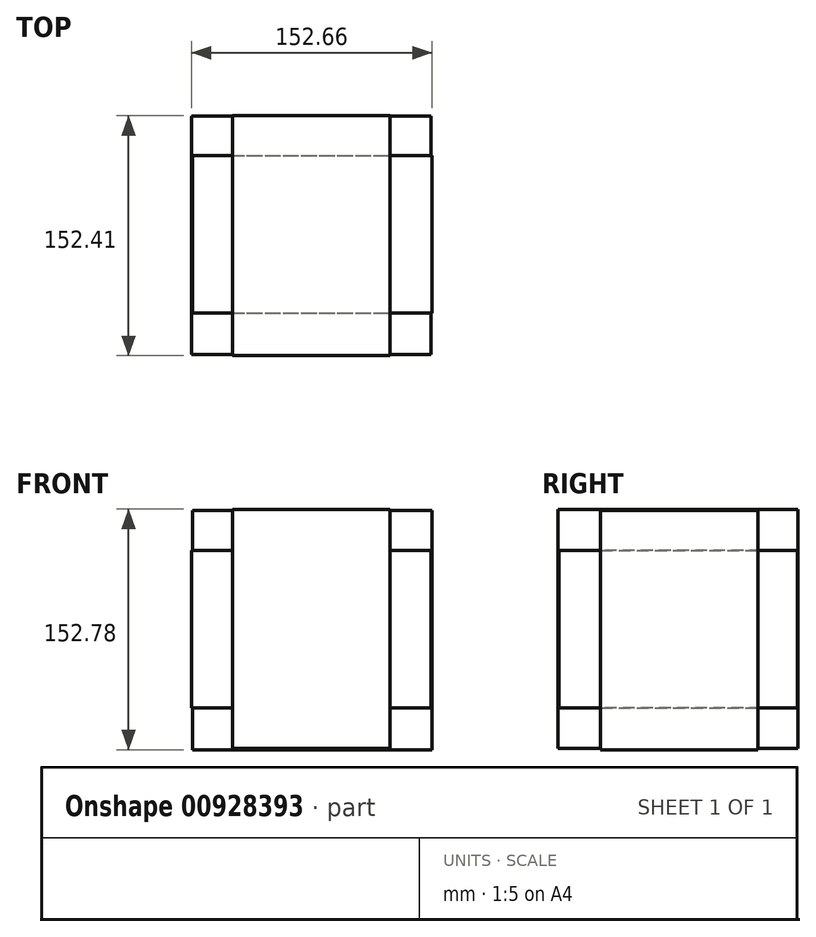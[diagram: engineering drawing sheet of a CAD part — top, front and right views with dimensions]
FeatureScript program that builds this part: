
annotation { "Feature Type Name" : "Feature", "Feature Type Description" : "" }
export const myFeature = defineFeature(function(context is Context, id is Id, definition is map)
    precondition{}
    {
        {
            var Q0;
            Q0=qCreatedBy(makeId("Front.planeOp"),FACE);
            var sketch = newSketch(context, id + "F0", { "sketchPlane" : qUnion([Q0])});
            skLineSegment(sketch, "E0.bottom", {"start": v(-75.57, 75.35) * mm, "end": v(76.58, 75.35) * mm});
            skLineSegment(sketch, "E0.top", {"start": v(-75.57, -76.57) * mm, "end": v(76.58, -76.57) * mm});
            skLineSegment(sketch, "E0.left", {"start": v(-75.57, 75.35) * mm, "end": v(-75.57, -76.57) * mm});
            skLineSegment(sketch, "E0.right", {"start": v(76.58, 75.35) * mm, "end": v(76.58, -76.57) * mm});
            skSolve(sketch);
        }
        {
            var Q0;
            Q0=qCreatedBy(makeId("Top.planeOp"),FACE);
            var sketch = newSketch(context, id + "F1", { "sketchPlane" : qUnion([Q0])});
            skLineSegment(sketch, "E1.bottom", {"start": v(-76.08, 75.1) * mm, "end": v(75.93, 75.1) * mm});
            skLineSegment(sketch, "E1.top", {"start": v(-76.08, -76.52) * mm, "end": v(75.93, -76.52) * mm});
            skLineSegment(sketch, "E1.left", {"start": v(-76.08, 75.1) * mm, "end": v(-76.08, -76.52) * mm});
            skLineSegment(sketch, "E1.right", {"start": v(75.93, 75.1) * mm, "end": v(75.93, -76.52) * mm});
            skSolve(sketch);
        }
        {
            var Q0;
            Q0=qCreatedBy(makeId("Right.planeOp"),FACE);
            var sketch = newSketch(context, id + "F2", { "sketchPlane" : qUnion([Q0])});
            skLineSegment(sketch, "E2.bottom", {"start": v(75.27, 76.2) * mm, "end": v(-77.14, 76.2) * mm});
            skLineSegment(sketch, "E2.top", {"start": v(75.27, -75.68) * mm, "end": v(-77.14, -75.68) * mm});
            skLineSegment(sketch, "E2.left", {"start": v(75.27, 76.2) * mm, "end": v(75.27, -75.68) * mm});
            skLineSegment(sketch, "E2.right", {"start": v(-77.14, 76.2) * mm, "end": v(-77.14, -75.68) * mm});
            skSolve(sketch);
        }
        {
            var Q0;
            Q0=makeQuery(id+"F1.imprint","IMPRINT",FACE,{"disambiguationData":[TD([[makeQuery(id+"F1.imprint","IMPRINT",EDGE,{"derivedFrom":sQuery(id+"F1.wireOp",EDGE,"E1.bottom")}),-1.0]])]});
            extrude(context, id + "F3", {"entities" : qUnion([Q0]), "depth" : 50 * mm, "offsetDistance" : 25.4 * mm, "hasSecondDirection" : true, "secondDirectionOppositeDirection" : true, "secondDirectionDepth" : 50 * mm});
        }
        {
            var Q0;
            Q0=makeQuery(id+"F0.imprint","IMPRINT",FACE,{"disambiguationData":[TD([[makeQuery(id+"F0.imprint","IMPRINT",EDGE,{"derivedFrom":sQuery(id+"F0.wireOp",EDGE,"E0.bottom")}),-1.0]])]});
            extrude(context, id + "F4", {"entities" : qUnion([Q0]), "operationType" : NewBodyOperationType.ADD, "depth" : 50 * mm, "offsetDistance" : 25.4 * mm, "hasSecondDirection" : true, "secondDirectionOppositeDirection" : true, "secondDirectionDepth" : 50 * mm});
        }
        {
            var Q0;
            Q0=makeQuery(id+"F2.imprint","IMPRINT",FACE,{"disambiguationData":[TD([[makeQuery(id+"F2.imprint","IMPRINT",EDGE,{"derivedFrom":sQuery(id+"F2.wireOp",EDGE,"E2.bottom")}),1.0]])]});
            extrude(context, id + "F5", {"entities" : qUnion([Q0]), "operationType" : NewBodyOperationType.ADD, "depth" : 50 * mm, "offsetDistance" : 25.4 * mm, "hasSecondDirection" : true, "secondDirectionOppositeDirection" : true, "secondDirectionDepth" : 50 * mm});
        }
        {
            var Q0;
            Q0=makeQuery(id+"F4.opExtrude","SWEPT_FACE",FACE,{"disambiguationData":[OSD([sQuery(id+"F0.wireOp",EDGE,"E0.right")])]});
            var sketch = newSketch(context, id + "F6", { "sketchPlane" : qUnion([Q0])});
            skCircle(sketch, "E3", {"center": v(0, 0) * mm, "radius": 41.93 * mm});
            skSolve(sketch);
        }
        {
            var Q0;
            Q0=sQuery(id+"F6.wireOp",EDGE,"E3");
            extrude(context, id + "F7", {"bodyType" : ToolBodyType.SURFACE, "surfaceEntities" : qUnion([Q0]), "depth" : 20 * mm, "offsetDistance" : 25.4 * mm});
        }
        {
            var Q0;
            Q0=makeQuery(id+"F5.opExtrude","SWEPT_FACE",FACE,{"disambiguationData":[OSD([sQuery(id+"F2.wireOp",EDGE,"E2.left")])]});
            var sketch = newSketch(context, id + "F8", { "sketchPlane" : qUnion([Q0])});
            skCircle(sketch, "E4", {"center": v(-23.84, 38.23) * mm, "radius": 22.49 * mm});
            skCircle(sketch, "E5", {"center": v(24.85, -26.5) * mm, "radius": 22.35 * mm});
            skSolve(sketch);
        }
        {
            var Q0;
            Q0=sQuery(id+"F8.wireOp",EDGE,"E4");
            var Q1;
            Q1=sQuery(id+"F8.wireOp",EDGE,"E5");
            extrude(context, id + "F9", {"bodyType" : ToolBodyType.SURFACE, "surfaceEntities" : qUnion([Q0, Q1]), "depth" : 20 * mm, "offsetDistance" : 25.4 * mm});
        }
        {
            var Q0;
            Q0=makeQuery(id+"F3.opExtrude","SWEPT_FACE",FACE,{"disambiguationData":[OSD([sQuery(id+"F1.wireOp",EDGE,"E1.left")])]});
            var sketch = newSketch(context, id + "F10", { "sketchPlane" : qUnion([Q0])});
            skCircle(sketch, "E6", {"center": v(-44.67, -27.62) * mm, "radius": 25.92 * mm});
            skCircle(sketch, "E7", {"center": v(42, -28.46) * mm, "radius": 25.99 * mm});
            skCircle(sketch, "E8", {"center": v(0, 30.64) * mm, "radius": 26.46 * mm});
            skSolve(sketch);
        }
        {
            var Q0;
            Q0=sQuery(id+"F10.wireOp",EDGE,"E8");
            var Q1;
            Q1=sQuery(id+"F10.wireOp",EDGE,"E6");
            var Q2;
            Q2=sQuery(id+"F10.wireOp",EDGE,"E7");
            extrude(context, id + "F11", {"bodyType" : ToolBodyType.SURFACE, "surfaceEntities" : qUnion([Q0, Q1, Q2]), "depth" : 20 * mm, "offsetDistance" : 25.4 * mm});
        }
        {
            var Q0;
            Q0=makeQuery(id+"F5.opExtrude","SWEPT_FACE",FACE,{"disambiguationData":[OSD([sQuery(id+"F2.wireOp",EDGE,"E2.right")])]});
            var sketch = newSketch(context, id + "F12", { "sketchPlane" : qUnion([Q0])});
            skCircle(sketch, "E9", {"center": v(-24.66, 28.1) * mm, "radius": 24.77 * mm});
            skCircle(sketch, "E10", {"center": v(27.69, 26.98) * mm, "radius": 25.33 * mm});
            skCircle(sketch, "E11", {"center": v(-21.56, -25.09) * mm, "radius": 24.77 * mm});
            skCircle(sketch, "E12", {"center": v(30.45, -27.57) * mm, "radius": 24.77 * mm});
            skSolve(sketch);
        }
        {
            var Q0;
            Q0=sQuery(id+"F12.wireOp",EDGE,"E9");
            var Q1;
            Q1=sQuery(id+"F12.wireOp",EDGE,"E10");
            var Q2;
            Q2=sQuery(id+"F12.wireOp",EDGE,"E11");
            var Q3;
            Q3=sQuery(id+"F12.wireOp",EDGE,"E12");
            extrude(context, id + "F13", {"bodyType" : ToolBodyType.SURFACE, "surfaceEntities" : qUnion([Q0, Q1, Q2, Q3]), "depth" : 20 * mm, "offsetDistance" : 25.4 * mm});
        }
    });
